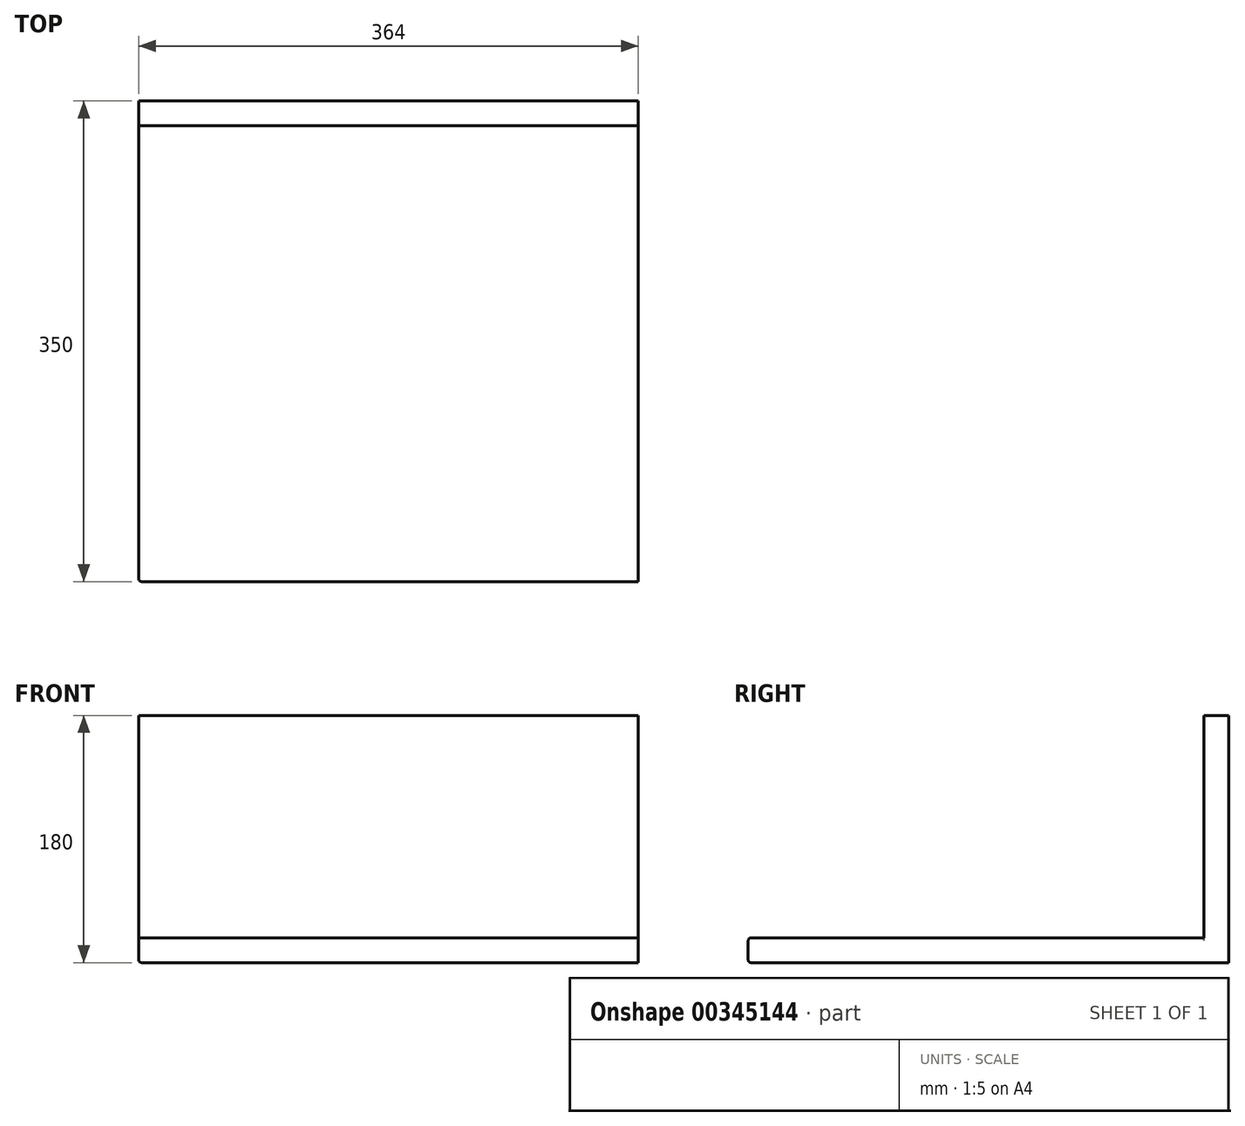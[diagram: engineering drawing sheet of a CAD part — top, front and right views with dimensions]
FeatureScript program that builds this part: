
annotation { "Feature Type Name" : "Feature", "Feature Type Description" : "" }
export const myFeature = defineFeature(function(context is Context, id is Id, definition is map)
    precondition{}
    {
        {
            var Q0;
            Q0=qCreatedBy(makeId("Front.planeOp"),FACE);
            var sketch = newSketch(context, id + "F0", { "sketchPlane" : qUnion([Q0])});
            skLineSegment(sketch, "E0.bottom", {"start": v(0, 0) * mm, "end": v(37.18, 0) * mm});
            skLineSegment(sketch, "E0.top", {"start": v(0, 34.03) * mm, "end": v(37.18, 34.03) * mm});
            skLineSegment(sketch, "E0.left", {"start": v(0, 0) * mm, "end": v(0, 34.03) * mm});
            skLineSegment(sketch, "E0.right", {"start": v(37.18, 0) * mm, "end": v(37.18, 34.03) * mm});
            skSolve(sketch);
        }
        {
            var Q0;
            Q0=makeQuery(id+"F0.imprint","IMPRINT",FACE,{"disambiguationData":[TD([[makeQuery(id+"F0.imprint","IMPRINT",EDGE,{"derivedFrom":sQuery(id+"F0.wireOp",EDGE,"E0.bottom")}),1.0]])]});
            extrude(context, id + "F1", {"entities" : qUnion([Q0]), "depth" : 350 * mm});
        }
        {
            var Q0;
            Q0=makeQuery(id+"F1.opExtrude","SWEPT_FACE",FACE,{"disambiguationData":[OSD([sQuery(id+"F0.wireOp",EDGE,"E0.left")])]});
            extrude(context, id + "F2", {"entities" : qUnion([Q0]), "operationType" : NewBodyOperationType.ADD, "oppositeDirection" : true, "depth" : 400 * mm});
        }
        {
            var Q0;
            {var subQ0=sQuery(id+"F0.wireOp",EDGE,"E0.bottom");Q0=makeQuery(id+"F2.boolean.opBoolean","MERGE",FACE,{"derivedFrom":[makeQuery(id+"F1.opExtrude","SWEPT_FACE",FACE,{"disambiguationData":[OSD([subQ0])]}),makeQuery(id+"F2.opExtrude","SWEPT_FACE",FACE,{"disambiguationData":[OSD([subQ0,sQuery(id+"F0.wireOp",EDGE,"E0.left")])]})]});}
            extrude(context, id + "F3", {"entities" : qUnion([Q0]), "operationType" : NewBodyOperationType.ADD, "oppositeDirection" : true, "depth" : 180 * mm});
        }
        {
            var Q0;
            {var subQ0=sQuery(id+"F0.wireOp",EDGE,"E0.left");var subQ1=sQuery(id+"F0.wireOp",EDGE,"E0.bottom");Q0=makeQuery(id+"F3.boolean.opBoolean","MERGE",FACE,{"derivedFrom":[makeQuery(id+"F1.opExtrude","SWEPT_FACE",FACE,{"disambiguationData":[OSD([subQ0])]}),makeQuery(id+"F3.opExtrude","SWEPT_FACE",FACE,{"disambiguationData":[OSD([subQ1,subQ0]),TDD([makeQuery(id+"F1.opExtrude","SWEPT_EDGE",EDGE,{"disambiguationData":[OSD([subQ1,subQ0])]})])]})]});}
            var Q1;
            {var subQ0=sQuery(id+"F0.wireOp",EDGE,"E0.left");var subQ1=sQuery(id+"F0.wireOp",EDGE,"E0.bottom");Q1=makeQuery(id+"F3.boolean.opBoolean","MERGE",FACE,{"derivedFrom":[makeQuery(id+"F2.boolean.opBoolean","MERGE",FACE,{"derivedFrom":[makeQuery(id+"F1.opExtrude","CAP_FACE",FACE,{"disambiguationData":[OSD([subQ1,sQuery(id+"F0.wireOp",EDGE,"E0.top"),subQ0,sQuery(id+"F0.wireOp",EDGE,"E0.right")])],"isStart":false}),makeQuery(id+"F2.opExtrude","SWEPT_FACE",FACE,{"disambiguationData":[OSD([subQ0]),TDD([makeQuery(id+"F1.opExtrude","CAP_EDGE",EDGE,{"disambiguationData":[OSD([subQ0])],"isStart":false})])]})]}),makeQuery(id+"F3.opExtrude","SWEPT_FACE",FACE,{"disambiguationData":[OSD([subQ1,subQ0]),TDD([makeQuery(id+"F2.boolean.opBoolean","MERGE",EDGE,{"derivedFrom":[makeQuery(id+"F1.opExtrude","CAP_EDGE",EDGE,{"disambiguationData":[OSD([subQ1])],"isStart":false}),makeQuery(id+"F2.opExtrude","SWEPT_EDGE",EDGE,{"disambiguationData":[OSD([subQ1,subQ0]),TDD([makeQuery(id+"F1.opExtrude","CAP_VERTEX",VERTEX,{"disambiguationData":[OSD([subQ1,subQ0])],"isStart":false})])]})]})])]})]});}
            var Q2;
            Q2=makeQuery(id+"F3.opExtrude","CAP_FACE",FACE,{"disambiguationData":[OSD([sQuery(id+"F0.wireOp",EDGE,"E0.bottom"),sQuery(id+"F0.wireOp",EDGE,"E0.left")])],"isStart":false});
            var Q3;
            {var subQ0=sQuery(id+"F0.wireOp",EDGE,"E0.left");var subQ1=sQuery(id+"F0.wireOp",EDGE,"E0.bottom");Q3=makeQuery(id+"F3.boolean.opBoolean","MERGE",FACE,{"derivedFrom":[makeQuery(id+"F2.opExtrude","CAP_FACE",FACE,{"disambiguationData":[OSD([subQ0])],"isStart":false}),makeQuery(id+"F3.opExtrude","SWEPT_FACE",FACE,{"disambiguationData":[OSD([subQ1,subQ0]),TDD([makeQuery(id+"F2.opExtrude","CAP_EDGE",EDGE,{"disambiguationData":[OSD([subQ1,subQ0])],"isStart":false})])]})]});}
            shell(context, id + "F4", {"entities" : qUnion([Q0, Q1, Q2, Q3]), "thickness" : 18 * mm});
        }
        {
            var Q0;
            {var subQ0=sQuery(id+"F0.wireOp",EDGE,"E0.left");var subQ1=sQuery(id+"F0.wireOp",EDGE,"E0.bottom");Q0=makeQuery(id+"F3.boolean.opBoolean","MERGE",FACE,{"derivedFrom":[makeQuery(id+"F2.opExtrude","CAP_FACE",FACE,{"disambiguationData":[OSD([subQ0])],"isStart":false}),makeQuery(id+"F3.opExtrude","SWEPT_FACE",FACE,{"disambiguationData":[OSD([subQ1,subQ0]),TDD([makeQuery(id+"F2.opExtrude","CAP_EDGE",EDGE,{"disambiguationData":[OSD([subQ1,subQ0])],"isStart":false})])]})]});}
            extrude(context, id + "F5", {"entities" : qUnion([Q0]), "operationType" : NewBodyOperationType.REMOVE, "oppositeDirection" : true, "depth" : 36 * mm});
        }
        {
            var Q0;
            {var subQ0=sQuery(id+"F0.wireOp",EDGE,"E0.left");var subQ1=sQuery(id+"F0.wireOp",EDGE,"E0.bottom");Q0=makeQuery(id+"F2.boolean.opBoolean","MERGE",EDGE,{"derivedFrom":[makeQuery(id+"F1.opExtrude","CAP_EDGE",EDGE,{"disambiguationData":[OSD([subQ1])],"isStart":false}),makeQuery(id+"F2.opExtrude","SWEPT_EDGE",EDGE,{"disambiguationData":[OSD([subQ1,subQ0]),TDD([makeQuery(id+"F1.opExtrude","CAP_VERTEX",VERTEX,{"disambiguationData":[OSD([subQ1,subQ0])],"isStart":false})])]})]});}
            fillet(context, id + "F6", {"entities" : qUnion([Q0]), "radius" : 2 * mm, "tangentPropagation" : true, "allowEdgeOverflow" : false});
        }
        {
            var Q0;
            {var subQ0=sQuery(id+"F0.wireOp",EDGE,"E0.left");var subQ1=sQuery(id+"F0.wireOp",EDGE,"E0.bottom");Q0=makeQuery(id+"F5.boolean.opBoolean","COPY",EDGE,{"derivedFrom":makeQuery(id+"F5.opExtrude","CAP_EDGE",EDGE,{"disambiguationData":[OSD([subQ1,subQ0]),TDD([makeQuery(id+"F3.boolean.opBoolean","MERGE",EDGE,{"derivedFrom":[makeQuery(id+"F2.opExtrude","CAP_EDGE",EDGE,{"disambiguationData":[OSD([subQ0]),TDD([makeQuery(id+"F1.opExtrude","CAP_EDGE",EDGE,{"disambiguationData":[OSD([subQ0])],"isStart":false})])],"isStart":false}),makeQuery(id+"F3.opExtrude","SWEPT_EDGE",EDGE,{"disambiguationData":[OSD([subQ1,subQ0]),TDD([makeQuery(id+"F2.opExtrude","CAP_VERTEX",VERTEX,{"disambiguationData":[OSD([subQ1,subQ0]),TDD([makeQuery(id+"F1.opExtrude","CAP_VERTEX",VERTEX,{"disambiguationData":[OSD([subQ1,subQ0])],"isStart":false})])],"isStart":false})])]})]})])],"isStart":false})});}
            var Q1;
            {var subQ0=sQuery(id+"F0.wireOp",EDGE,"E0.left");var subQ1=sQuery(id+"F0.wireOp",EDGE,"E0.bottom");Q1=makeQuery(id+"F3.boolean.opBoolean","MERGE",EDGE,{"derivedFrom":[makeQuery(id+"F1.opExtrude","CAP_EDGE",EDGE,{"disambiguationData":[OSD([subQ0])],"isStart":false}),makeQuery(id+"F3.opExtrude","SWEPT_EDGE",EDGE,{"disambiguationData":[OSD([subQ1,subQ0]),TDD([makeQuery(id+"F1.opExtrude","CAP_VERTEX",VERTEX,{"disambiguationData":[OSD([subQ1,subQ0])],"isStart":false})])]})]});}
            fillet(context, id + "F7", {"entities" : qUnion([Q0, Q1]), "radius" : 2 * mm, "tangentPropagation" : true, "allowEdgeOverflow" : false});
        }
        {
            var Q0;
            {var subQ0=sQuery(id+"F0.wireOp",EDGE,"E0.left");var subQ1=sQuery(id+"F0.wireOp",EDGE,"E0.bottom");Q0=makeQuery(id+"F4.opShell","OFFSET_EDGE",EDGE,{"disambiguationData":[OSD([subQ1,subQ0]),TDD([makeQuery(id+"F2.boolean.opBoolean","MERGE",EDGE,{"derivedFrom":[makeQuery(id+"F1.opExtrude","CAP_EDGE",EDGE,{"disambiguationData":[OSD([subQ1])],"isStart":false}),makeQuery(id+"F2.opExtrude","SWEPT_EDGE",EDGE,{"disambiguationData":[OSD([subQ1,subQ0]),TDD([makeQuery(id+"F1.opExtrude","CAP_VERTEX",VERTEX,{"disambiguationData":[OSD([subQ1,subQ0])],"isStart":false})])]})]})])]});}
            fillet(context, id + "F8", {"entities" : qUnion([Q0]), "radius" : 2 * mm, "tangentPropagation" : true, "allowEdgeOverflow" : false});
        }
    });
